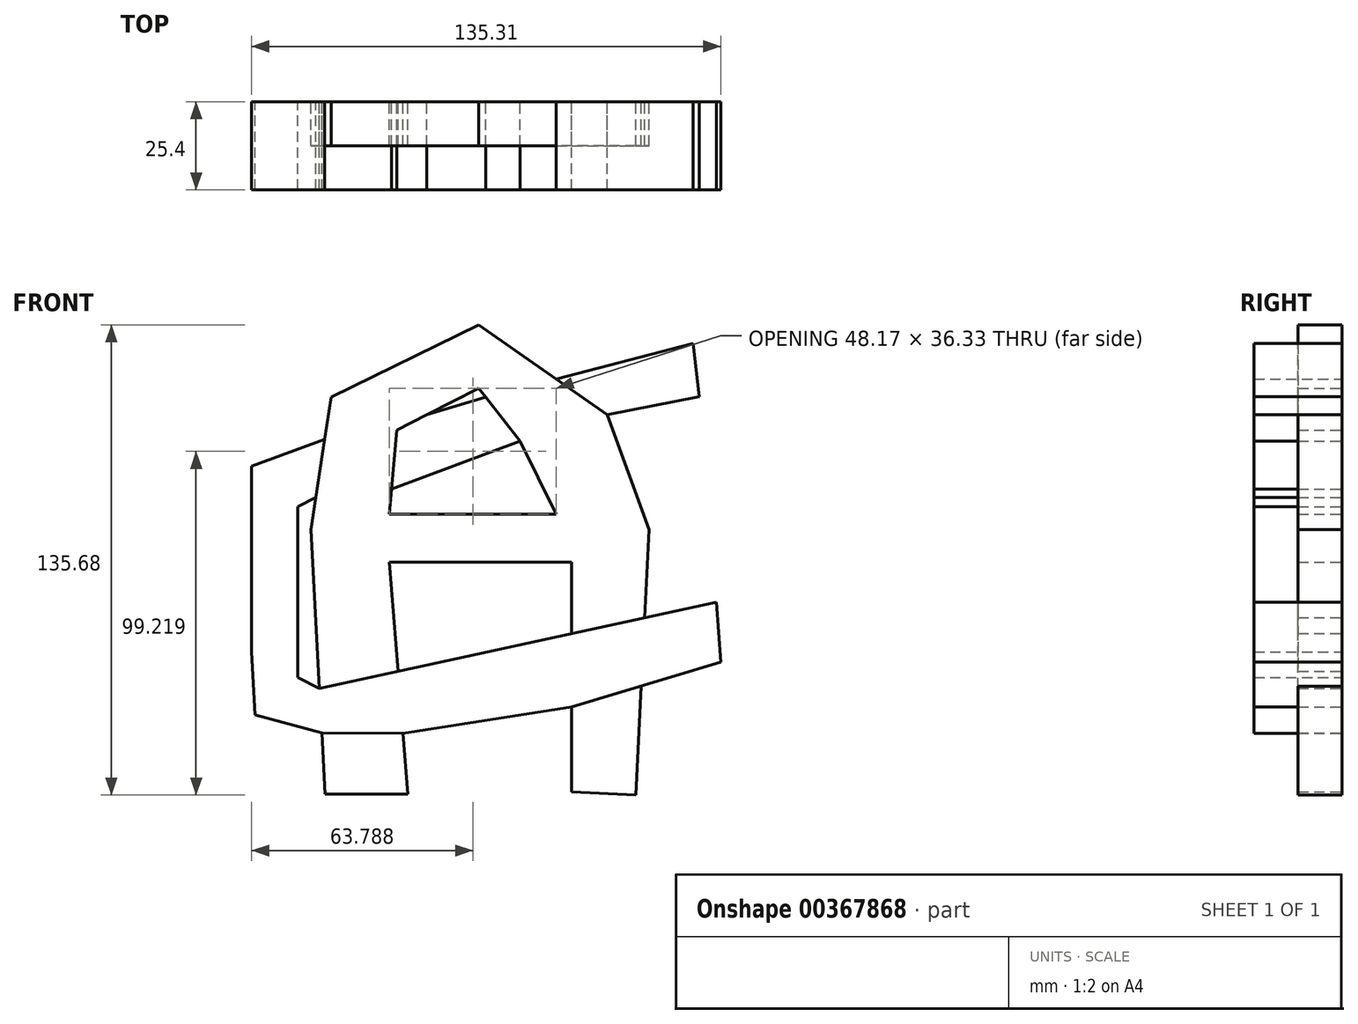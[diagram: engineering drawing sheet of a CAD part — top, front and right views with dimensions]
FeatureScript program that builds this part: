
annotation { "Feature Type Name" : "Feature", "Feature Type Description" : "" }
export const myFeature = defineFeature(function(context is Context, id is Id, definition is map)
    precondition{}
    {
        {
            var Q0;
            Q0=qCreatedBy(makeId("Front.planeOp"),FACE);
            var sketch = newSketch(context, id + "F0", { "sketchPlane" : qUnion([Q0])});
            skLineSegment(sketch, "E0", {"start": v(-48.46, 0) * mm, "end": v(-42.59, 38.18) * mm});
            skLineSegment(sketch, "E1", {"start": v(-42.59, 38.18) * mm, "end": v(0, 59.03) * mm});
            skLineSegment(sketch, "E2", {"start": v(0, 59.03) * mm, "end": v(37, 33.19) * mm});
            skLineSegment(sketch, "E3", {"start": v(37, 33.19) * mm, "end": v(49.05, 0) * mm});
            skLineSegment(sketch, "E4", {"start": v(49.05, 0) * mm, "end": v(47.78, -25.47) * mm});
            skLineSegment(sketch, "E5", {"start": v(45.23, -76.65) * mm, "end": v(26.77, -75.73) * mm});
            skLineSegment(sketch, "E6", {"start": v(26.77, -75.73) * mm, "end": v(26.77, -51.2) * mm});
            skLineSegment(sketch, "E7", {"start": v(26.77, -9.4) * mm, "end": v(-25.85, -9.4) * mm});
            skLineSegment(sketch, "E8", {"start": v(-25.85, -9.4) * mm, "end": v(-23.36, -40.94) * mm});
            skLineSegment(sketch, "E9", {"start": v(-20.56, -76.36) * mm, "end": v(-44.35, -76.36) * mm});
            skLineSegment(sketch, "E10", {"start": v(-44.35, -76.36) * mm, "end": v(-45.3, -58.73) * mm});
            skLineSegment(sketch, "E11", {"start": v(-25.85, 4.4) * mm, "end": v(22.32, 4.4) * mm});
            skLineSegment(sketch, "E12", {"start": v(22.32, 4.4) * mm, "end": v(11.9, 25.46) * mm});
            skLineSegment(sketch, "E13", {"start": v(11.9, 25.46) * mm, "end": v(0, 40.73) * mm});
            skLineSegment(sketch, "E14", {"start": v(0, 40.73) * mm, "end": v(-23.64, 28.7) * mm});
            skLineSegment(sketch, "E15", {"start": v(-23.64, 28.7) * mm, "end": v(-25.85, 4.4) * mm});
            skLineSegment(sketch, "E16", {"start": v(61.83, 53.66) * mm, "end": v(22.32, 43.44) * mm});
            skLineSegment(sketch, "E17", {"start": v(22.32, 43.44) * mm, "end": v(37, 33.19) * mm});
            skLineSegment(sketch, "E18", {"start": v(37, 33.19) * mm, "end": v(63.59, 38.32) * mm});
            skPoint(sketch, "E18.endSnap0", {"position": v(29.66, 38.32) * mm});
            skLineSegment(sketch, "E19", {"start": v(63.59, 38.32) * mm, "end": v(61.83, 53.66) * mm});
            skLineSegment(sketch, "E20", {"start": v(-44.47, 25.95) * mm, "end": v(-65.55, 18.3) * mm});
            skLineSegment(sketch, "E21", {"start": v(-65.55, 18.3) * mm, "end": v(-65.55, -35.33) * mm});
            skLineSegment(sketch, "E22", {"start": v(-65.55, -35.33) * mm, "end": v(-64.57, -53.44) * mm});
            skLineSegment(sketch, "E23", {"start": v(-64.57, -53.44) * mm, "end": v(-45.3, -58.73) * mm});
            skLineSegment(sketch, "E24", {"start": v(-21.94, -58.83) * mm, "end": v(26.77, -51.2) * mm});
            skLineSegment(sketch, "E25", {"start": v(46.8, -45.17) * mm, "end": v(69.76, -38.27) * mm});
            skLineSegment(sketch, "E26", {"start": v(2, 38.16) * mm, "end": v(-14.99, 33.1) * mm});
            skPoint(sketch, "E26.endSnap0", {"position": v(5.95, 33.1) * mm});
            skLineSegment(sketch, "E27", {"start": v(11.9, 25.46) * mm, "end": v(-25.19, 11.64) * mm});
            skLineSegment(sketch, "E28", {"start": v(-47.04, 9.25) * mm, "end": v(-52.22, 6.6) * mm});
            skLineSegment(sketch, "E29", {"start": v(-52.22, 6.6) * mm, "end": v(-52.22, -17.42) * mm});
            skLineSegment(sketch, "E30", {"start": v(-52.22, -17.42) * mm, "end": v(-52.22, -34.75) * mm});
            skLineSegment(sketch, "E31", {"start": v(-52.22, -34.75) * mm, "end": v(-52.22, -42.68) * mm});
            skLineSegment(sketch, "E32", {"start": v(-52.22, -42.68) * mm, "end": v(-45.99, -45.86) * mm});
            skLineSegment(sketch, "E33", {"start": v(-45.99, -45.86) * mm, "end": v(68.58, -20.94) * mm});
            skLineSegment(sketch, "E34", {"start": v(68.58, -20.94) * mm, "end": v(69.76, -38.27) * mm});
            skLineSegment(sketch, "E35", {"start": v(-45.3, -58.73) * mm, "end": v(-21.94, -58.83) * mm});
            skLineSegment(sketch, "E36", {"start": v(26.77, -51.2) * mm, "end": v(49.85, -44.26) * mm});
            skLineSegment(sketch, "E37.trimOffspring", {"start": v(-45.99, -45.86) * mm, "end": v(-48.46, 0) * mm});
            skLineSegment(sketch, "E38.trimOffspring", {"start": v(-21.94, -58.83) * mm, "end": v(-20.56, -76.36) * mm});
            skLineSegment(sketch, "E39.trimOffspring", {"start": v(26.77, -30.04) * mm, "end": v(26.77, -9.4) * mm});
            skLineSegment(sketch, "E40.trimOffspring", {"start": v(46.8, -45.17) * mm, "end": v(45.23, -76.65) * mm});
            skSolve(sketch);
        }
        {
            var Q0;
            {var subQ3=sQuery(id+"F0.wireOp",EDGE,"E20");Q0=makeQuery(id+"F0.imprint","IMPRINT",FACE,{"disambiguationData":[TD([[makeQuery(id+"F0.imprint","IMPRINT",EDGE,{"derivedFrom":subQ3}),1.0]])]});}
            var Q1;
            {var subQ0=sQuery(id+"F0.wireOp",EDGE,"E26");Q1=makeQuery(id+"F0.imprint","IMPRINT",FACE,{"disambiguationData":[TD([[makeQuery(id+"F0.imprint","IMPRINT",EDGE,{"derivedFrom":subQ0}),1.0]])]});}
            var Q2;
            Q2=makeQuery(id+"F0.imprint","IMPRINT",FACE,{"disambiguationData":[TD([[makeQuery(id+"F0.imprint","IMPRINT",EDGE,{"derivedFrom":sQuery(id+"F0.wireOp",EDGE,"E16")}),1.0]])]});
            extrude(context, id + "F1", {"entities" : qUnion([Q0, Q1, Q2]), "depth" : 25.4 * mm});
        }
        {
            var Q0;
            {var subQ7=sQuery(id+"F0.wireOp",EDGE,"E1");Q0=makeQuery(id+"F0.imprint","IMPRINT",FACE,{"disambiguationData":[TD([[makeQuery(id+"F0.imprint","IMPRINT",EDGE,{"derivedFrom":subQ7}),-1.0]])]});}
            var Q1;
            Q1=makeQuery(id+"F0.imprint","IMPRINT",FACE,{"disambiguationData":[TD([[makeQuery(id+"F0.imprint","IMPRINT",EDGE,{"derivedFrom":sQuery(id+"F0.wireOp",EDGE,"E5")}),-1.0]])]});
            var Q2;
            Q2=makeQuery(id+"F0.imprint","IMPRINT",FACE,{"disambiguationData":[TD([[makeQuery(id+"F0.imprint","IMPRINT",EDGE,{"derivedFrom":sQuery(id+"F0.wireOp",EDGE,"E9")}),-1.0]])]});
            extrude(context, id + "F2", {"entities" : qUnion([Q0, Q1, Q2]), "depth" : 12.7 * mm});
        }
    });
